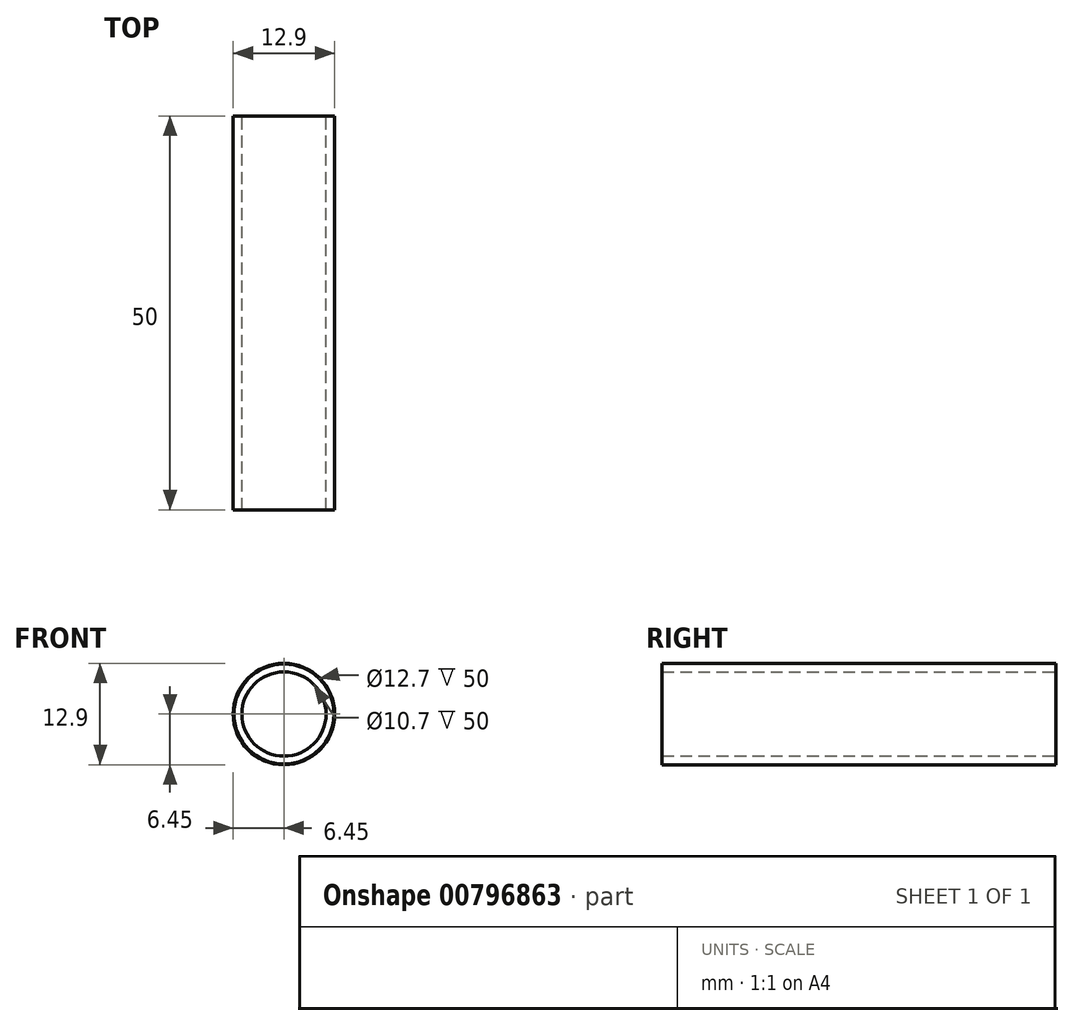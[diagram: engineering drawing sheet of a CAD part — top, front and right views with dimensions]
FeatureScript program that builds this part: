
annotation { "Feature Type Name" : "Feature", "Feature Type Description" : "" }
export const myFeature = defineFeature(function(context is Context, id is Id, definition is map)
    precondition{}
    {
        {
            var Q0;
            Q0=qCreatedBy(makeId("Front.planeOp"),FACE);
            var sketch = newSketch(context, id + "F0", { "sketchPlane" : qUnion([Q0])});
            skCircle(sketch, "E0", {"center": v(0, 0) * mm, "radius": 6.35 * mm});
            skCircle(sketch, "E1", {"center": v(0, 0) * mm, "radius": 5.35 * mm});
            skSolve(sketch);
        }
        {
            var Q0;
            Q0=makeQuery(id+"F0.imprint","IMPRINT",FACE,{"disambiguationData":[TD([[makeQuery(id+"F0.imprint","IMPRINT",EDGE,{"derivedFrom":sQuery(id+"F0.wireOp",EDGE,"E0")}),1.0]])]});
            extrude(context, id + "F1", {"entities" : qUnion([Q0]), "depth" : 50 * mm, "offsetDistance" : 25 * mm});
        }
        {
            var Q0;
            Q0=qCreatedBy(makeId("Front.planeOp"),FACE);
            var sketch = newSketch(context, id + "F2", { "sketchPlane" : qUnion([Q0])});
            skCircle(sketch, "E2", {"center": v(0, 0) * mm, "radius": 6.35 * mm});
            skCircle(sketch, "E3", {"center": v(0, 0) * mm, "radius": 6.45 * mm});
            skSolve(sketch);
        }
        {
            var Q0;
            Q0=makeQuery(id+"F2.imprint","IMPRINT",FACE,{"disambiguationData":[TD([[makeQuery(id+"F2.imprint","IMPRINT",EDGE,{"derivedFrom":sQuery(id+"F2.wireOp",EDGE,"E2")}),-1.0]])]});
            var Q1;
            Q1=makeQuery(id+"F1.opExtrude","CAP_FACE",FACE,{"disambiguationData":[OSD([sQuery(id+"F0.wireOp",EDGE,"E0"),sQuery(id+"F0.wireOp",EDGE,"E1")])],"isStart":false});
            extrude(context, id + "F3", {"entities" : qUnion([Q0]), "endBound" : BoundingType.UP_TO_SURFACE, "depth" : 25 * mm, "endBoundEntityFace" : qUnion([Q1]), "offsetDistance" : 25 * mm});
        }
    });
